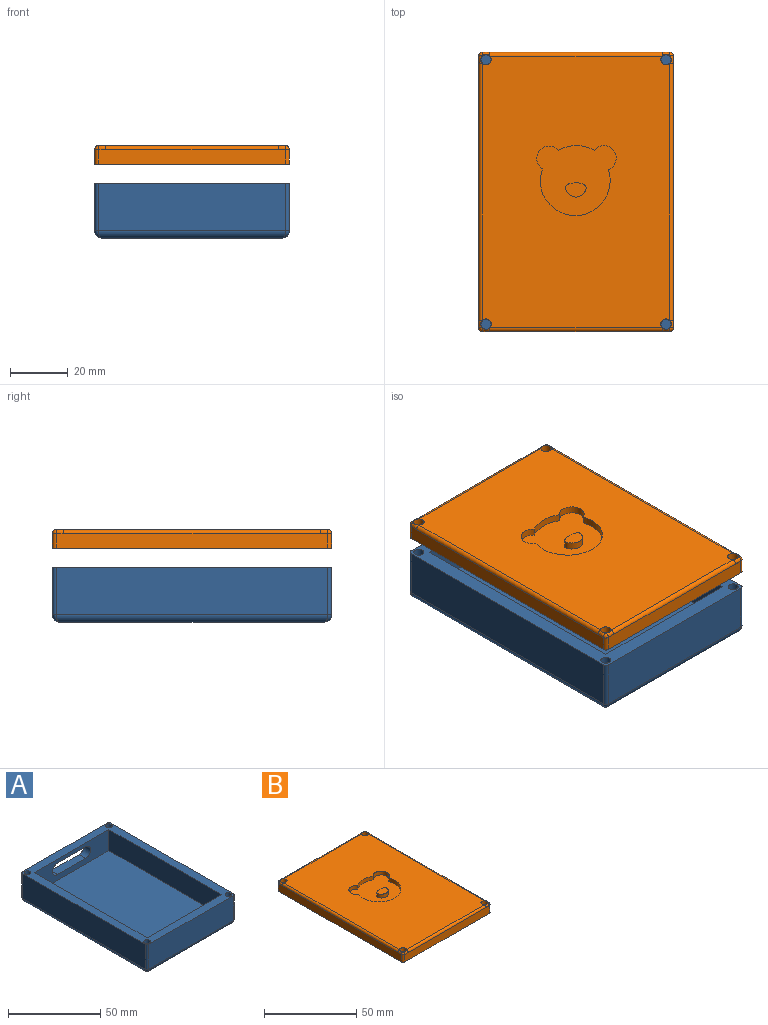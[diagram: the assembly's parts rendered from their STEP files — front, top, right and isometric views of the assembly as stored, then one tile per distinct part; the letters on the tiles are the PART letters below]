
ASSEMBLY  parts=2 mates=2
PART A: 35 faces, bbox 67.3x96.5x19.1 mm
  f0: plane 96.52x67.31mm, normal (0,0,1), area 1521.3mm2, adj f1,f2,f3,f4,f5,f6,f7,f8
  f1: plane 64.77x16.51mm, normal (0,1,0), area 859.2mm2, adj f0,f2,f8,f15,f16,f17,f18,f28
  f2: cylinder r=1.27mm len=16.51mm, axis (0,0,-1), area 32.9mm2, adj f0,f1,f3,f27
  f3: plane 93.98x16.51mm, normal (-1,0,0), area 1551.6mm2, adj f0,f2,f4,f29
  f4: cylinder r=1.27mm len=16.51mm, axis (0,0,-1), area 32.9mm2, adj f0,f3,f5,f31
  f5: plane 64.77x16.51mm, normal (0,-1,0), area 1069.4mm2, adj f0,f4,f6,f33
  f6: cylinder r=1.27mm len=16.51mm, axis (0,0,-1), area 32.9mm2, adj f0,f5,f7,f34
  f7: plane 93.98x16.51mm, normal (1,0,0), area 1551.6mm2, adj f0,f6,f8,f32
  f8: cylinder r=1.27mm len=16.51mm, axis (0,0,-1), area 32.9mm2, adj f0,f1,f7,f30
  f9: plane 91.44x62.23mm, normal (0,0,-1), area 5690.3mm2, adj f28,f29,f32,f33
  f10: plane 57.15x13.97mm, normal (0,-1,0), area 588.3mm2, adj f0,f11,f13,f14,f15,f16,f17,f18
  f11: plane 86.36x13.97mm, normal (1,0,0), area 1206.4mm2, adj f0,f10,f12,f14
  f12: plane 57.15x13.97mm, normal (0,1,0), area 798.4mm2, adj f0,f11,f13,f14
  f13: plane 86.36x13.97mm, normal (-1,0,0), area 1206.4mm2, adj f0,f10,f12,f14
  f14: plane 86.36x57.15mm, normal (0,0,1), area 4935.5mm2, adj f10,f11,f12,f13
  f15: cylinder r=3.81mm len=7.62mm, axis (0,1,0), area 60.8mm2, adj f1,f10,f16,f18
  f16: plane 21.59x5.08mm, normal (0,0,-1), area 109.7mm2, adj f1,f10,f15,f17
  f17: cylinder r=3.81mm len=7.62mm, axis (0,1,0), area 60.8mm2, adj f1,f10,f16,f18
  f18: plane 21.59x5.08mm, normal (0,0,1), area 109.7mm2, adj f1,f10,f15,f17
  f19: cylinder r=1.75mm len=9.53mm, axis (0,0,1), area 104.9mm2, adj f0,f20
  f20: plane 3.51x3.51mm, normal (0,0,1), area 9.6mm2, adj f19
  f21: cylinder r=1.75mm len=9.53mm, axis (0,0,1), area 104.9mm2, adj f0,f22
  f22: plane 3.51x3.51mm, normal (0,0,1), area 9.6mm2, adj f21
  f23: cylinder r=1.75mm len=9.53mm, axis (0,0,1), area 104.9mm2, adj f0,f24
  f24: plane 3.51x3.51mm, normal (0,0,1), area 9.6mm2, adj f23
  f25: cylinder r=1.75mm len=9.53mm, axis (0,0,1), area 104.9mm2, adj f0,f26
  f26: plane 3.51x3.51mm, normal (0,0,1), area 9.6mm2, adj f25
  f27: bspline ~3.03x2.54mm, area 5.3mm2, adj f2,f28,f29
  f28: cylinder r=2.54mm len=64.77mm, axis (-1,0,0), area 254.7mm2, adj f1,f9,f27,f30
  f29: cylinder r=2.54mm len=93.98mm, axis (0,-1,0), area 371.3mm2, adj f3,f9,f27,f31
  f30: bspline ~3.03x2.54mm, area 5.3mm2, adj f8,f28,f32
  f31: bspline ~3.03x2.54mm, area 5.3mm2, adj f4,f29,f33
  f32: cylinder r=2.54mm len=93.98mm, axis (0,1,0), area 371.3mm2, adj f7,f9,f30,f34
  f33: cylinder r=2.54mm len=64.77mm, axis (1,0,0), area 254.7mm2, adj f5,f9,f31,f34
  f34: bspline ~3.03x2.54mm, area 5.3mm2, adj f6,f32,f33
PART B: 37 faces, bbox 67.3x96.5x6.4 mm
  f0: plane 64.77x5.21mm, normal (0,1,0), area 329.4mm2, adj f1,f11,f13,f16,f18,f20
  f1: cylinder r=1.27mm len=5.08mm, axis (0,0,-1), area 10.1mm2, adj f0,f2,f13,f14
  f2: plane 93.98x5.21mm, normal (-1,0,0), area 477.8mm2, adj f1,f3,f13,f15,f17,f19
  f3: cylinder r=1.27mm len=5.08mm, axis (0,0,-1), area 10.1mm2, adj f2,f4,f13,f21
  f4: plane 64.77x5.21mm, normal (0,-1,0), area 329.4mm2, adj f3,f5,f13,f23,f25,f27
  f5: cylinder r=1.27mm len=5.08mm, axis (0,0,-1), area 10.1mm2, adj f4,f6,f13,f29
  f6: plane 93.98x5.21mm, normal (1,0,0), area 477.8mm2, adj f5,f11,f13,f24,f26,f28
  f7: cylinder r=1.83mm len=6.35mm, axis (0,0,-1), area 73mm2, adj f12,f13,f15,f16
  f8: cylinder r=1.83mm len=6.35mm, axis (0,0,-1), area 73mm2, adj f12,f13,f27,f28
  f9: cylinder r=1.83mm len=6.35mm, axis (0,0,-1), area 73mm2, adj f12,f13,f19,f23
  f10: cylinder r=1.83mm len=6.35mm, axis (0,0,-1), area 73mm2, adj f12,f13,f20,f24
  f11: cylinder r=1.27mm len=5.08mm, axis (0,0,-1), area 10.1mm2, adj f0,f6,f13,f22
  f12: plane 93.98x64.77mm, normal (0,0,1), area 5529.1mm2, adj f7,f8,f9,f10,f17,f18,f25,f26
  f13: plane 96.52x67.31mm, normal (0,0,-1), area 6453.3mm2, adj f0,f1,f2,f3,f4,f5,f6,f7
  f14: sphere r=1.27mm, area 2.5mm2, adj f1,f15,f16
  f15: bspline ~2.61x1.27mm, area 4.2mm2, adj f2,f7,f14,f17
  f16: bspline ~2.61x1.27mm, area 4.2mm2, adj f0,f7,f14,f18
  f17: cylinder r=1.27mm len=88.81mm, axis (0,1,0), area 177.2mm2, adj f2,f12,f15,f19
  f18: cylinder r=1.27mm len=59.6mm, axis (1,0,0), area 118.9mm2, adj f0,f12,f16,f20
  f19: bspline ~2.61x1.27mm, area 4.2mm2, adj f2,f9,f17,f21
  f20: bspline ~2.61x1.27mm, area 4.2mm2, adj f0,f10,f18,f22
  f21: sphere r=1.27mm, area 2.5mm2, adj f3,f19,f23
  f22: sphere r=1.27mm, area 2.5mm2, adj f11,f20,f24
  f23: bspline ~2.61x1.27mm, area 4.2mm2, adj f4,f9,f21,f25
  f24: bspline ~2.61x1.27mm, area 4.2mm2, adj f6,f10,f22,f26
  f25: cylinder r=1.27mm len=59.6mm, axis (-1,0,0), area 118.9mm2, adj f4,f12,f23,f27
  f26: cylinder r=1.27mm len=88.81mm, axis (0,-1,0), area 177.2mm2, adj f6,f12,f24,f28
  f27: bspline ~2.61x1.27mm, area 4.2mm2, adj f4,f8,f25,f29
  f28: bspline ~2.61x1.27mm, area 4.2mm2, adj f6,f8,f26,f29
  f29: sphere r=1.27mm, area 2.5mm2, adj f5,f27,f28
  f30: cylinder r=4.3mm len=8.31mm, axis (0,0,1), area 39.9mm2, adj f12,f31,f33,f35
  f31: cylinder r=12.89mm len=12.32mm, axis (0,0,1), area 32.6mm2, adj f12,f30,f32,f35
  f32: cylinder r=4.33mm len=7.94mm, axis (0,0,1), area 37.2mm2, adj f12,f31,f33,f35
  f33: cylinder r=12.06mm len=24.13mm, axis (0,0,1), area 116.7mm2, adj f12,f30,f32,f35
  f34: extruded ~7.13x4.95mm, area 48.6mm2, adj f35,f36
  f35: plane 27.45x24.22mm, normal (0,0,1), area 496.8mm2, adj f30,f31,f32,f33,f34
  f36: plane 7.91x5.71mm, normal (0,0,1), area 27.3mm2, adj f34
PLACE A t=(1.63,16.8,9.79)mm
PLACE B t=(1.63,16.8,35.33)mm
MATE planar B.f6 <-> A.f7  axis (1,0,0) through (68.94,65.06,37.88)mm
MATE planar B.f4 <-> A.f5  axis (0,-1,0) through (35.28,16.8,37.88)mm
